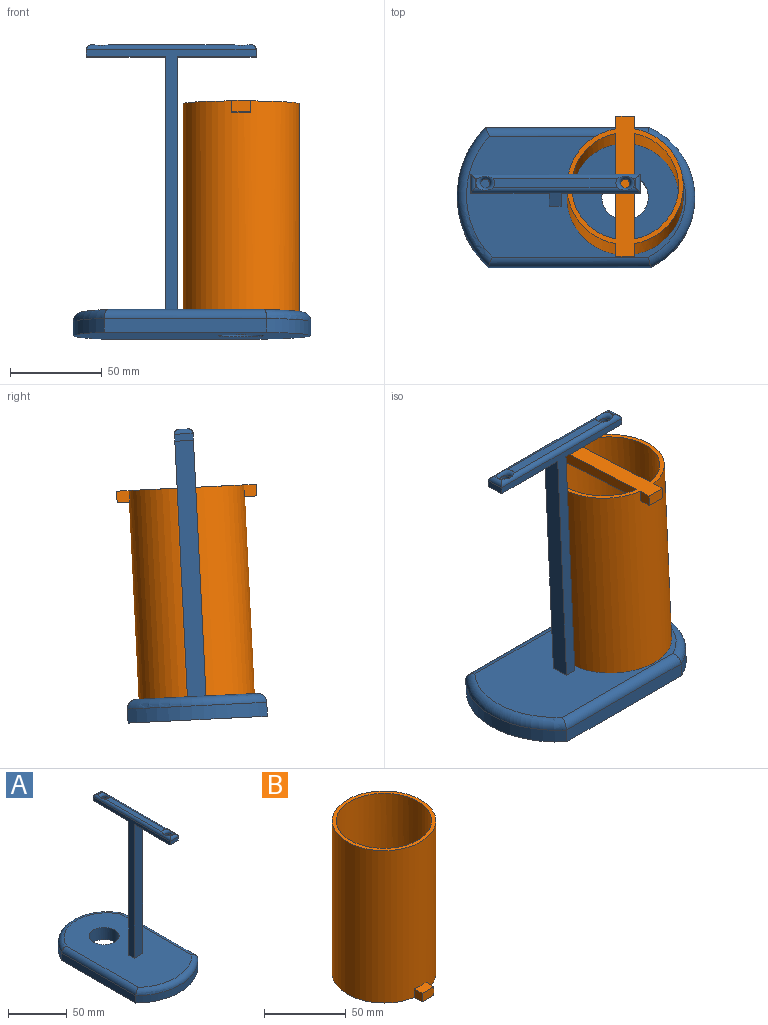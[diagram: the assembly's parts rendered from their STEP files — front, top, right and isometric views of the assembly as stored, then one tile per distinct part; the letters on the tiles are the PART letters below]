
ASSEMBLY  parts=2 mates=1
PART A: 30 faces, bbox 82.5x137.6x158.8 mm
  f0: plane 143.51x92.59mm, normal (1,0,0), area 1239.9mm2, adj f2,f3,f6,f7,f9,f12,f16,f23
  f1: plane 143.51x92.59mm, normal (-1,0,0), area 1239.9mm2, adj f2,f3,f6,f7,f9,f12,f17,f23
  f2: plane 139.7x10.16mm, normal (0,1,0), area 1419.4mm2, adj f0,f1,f12,f23
  f3: plane 139.7x10.16mm, normal (0,-1,0), area 1419.4mm2, adj f0,f1,f6,f23
  f4: plane 67.61x5.08mm, normal (0,0,1), area 338.8mm2, adj f15,f16,f17,f18
  f5: plane 5.08x1.15mm, normal (0,0,1), area 3.5mm2, adj f14,f15,f16,f17
  f6: plane 43.12x10.16mm, normal (0,0,-1), area 417.8mm2, adj f0,f1,f3,f9,f10
  f7: plane 10.16x3.81mm, normal (0,1,0), area 38.7mm2, adj f0,f1,f12,f14
  f8: cylinder r=2.54mm len=5.08mm, axis (0,0,-1), area 60.8mm2, adj f12,f15
  f9: plane 10.16x3.81mm, normal (0,-1,0), area 38.7mm2, adj f0,f1,f6,f13
  f10: cylinder r=2.54mm len=5.08mm, axis (0,0,-1), area 60.8mm2, adj f6,f18
  f11: plane 5.08x1.15mm, normal (0,0,1), area 3.5mm2, adj f13,f16,f17,f18
  f12: plane 43.12x10.16mm, normal (0,0,-1), area 417.8mm2, adj f0,f1,f2,f7,f8
  f13: cylinder r=2.54mm len=10.16mm, axis (-1,0,0), area 33.2mm2, adj f9,f11,f16,f17
  f14: cylinder r=2.54mm len=10.16mm, axis (1,0,0), area 33.2mm2, adj f5,f7,f16,f17
  f15: torus R=5.08mm, axis (0,0,1), area 69.5mm2, adj f4,f5,f8,f16,f17
  f16: cylinder r=2.54mm len=92.59mm, axis (0,-1,0), area 346.7mm2, adj f0,f4,f5,f11,f13,f14,f15,f18
  f17: cylinder r=2.54mm len=92.59mm, axis (0,1,0), area 346.7mm2, adj f1,f4,f5,f11,f13,f14,f15,f18
  f18: torus R=5.08mm, axis (0,0,1), area 69.5mm2, adj f4,f10,f11,f16,f17
  f19: cylinder r=52.78mm len=76.17mm, axis (0,0,-1), area 648.5mm2, adj f20,f22,f24,f28
  f20: plane 89.27x7.62mm, normal (-1,0,0), area 680.3mm2, adj f19,f21,f24,f29
  f21: cylinder r=41.78mm len=76.17mm, axis (0,0,-1), area 730.5mm2, adj f20,f22,f24,f27
  f22: plane 88.52x7.62mm, normal (1,0,0), area 674.5mm2, adj f19,f21,f24,f26
  f23: plane 119.6x66.01mm, normal (0,0,1), area 6662.4mm2, adj f0,f1,f2,f3,f25,f26,f27,f28
  f24: plane 129.76x76.17mm, normal (0,0,-1), area 8467.1mm2, adj f19,f20,f21,f22,f25
  f25: cylinder r=12.7mm len=25.4mm, axis (0,0,1), area 1013.4mm2, adj f23,f24
  f26: cylinder r=5.08mm len=88.52mm, axis (0,1,0), area 697.2mm2, adj f22,f23,f27,f28
  f27: torus R=36.7mm, axis (0,0,-1), area 724.9mm2, adj f21,f23,f26,f29
  f28: torus R=47.7mm, axis (0,0,-1), area 643.7mm2, adj f19,f23,f26,f29
  f29: cylinder r=5.08mm len=89.27mm, axis (0,-1,0), area 703mm2, adj f20,f23,f27,f28
PART B: 15 faces, bbox 63.5x76.4x114.3 mm
  f0: cylinder r=29.21mm len=114.3mm, axis (0,0,1), area 20848mm2, adj f2,f11,f12,f13,f14
  f1: cylinder r=31.75mm len=114.3mm, axis (0,0,1), area 22672.2mm2, adj f2,f3,f5,f6,f7,f8,f10,f14
  f2: plane 76.41x63.5mm, normal (0,0,-1), area 1210.9mm2, adj f0,f1,f3,f4,f5,f7,f8,f9
  f3: plane 6.86x6.35mm, normal (1,0,0), area 43.6mm2, adj f1,f2,f4,f6
  f4: plane 10.16x6.35mm, normal (0,-1,0), area 64.5mm2, adj f2,f3,f5,f6
  f5: plane 6.86x6.35mm, normal (-1,0,0), area 43.6mm2, adj f1,f2,f4,f6
  f6: plane 10.16x6.86mm, normal (0,0,1), area 66.9mm2, adj f1,f3,f4,f5
  f7: plane 6.86x6.35mm, normal (1,0,0), area 43.6mm2, adj f1,f2,f9,f10
  f8: plane 6.86x6.35mm, normal (-1,0,0), area 43.6mm2, adj f1,f2,f9,f10
  f9: plane 10.16x6.35mm, normal (0,1,0), area 64.5mm2, adj f2,f7,f8,f10
  f10: plane 10.16x6.86mm, normal (0,0,1), area 66.9mm2, adj f1,f7,f8,f9
  f11: plane 57.53x6.35mm, normal (1,0,0), area 365.3mm2, adj f0,f2,f13
  f12: plane 57.53x6.35mm, normal (-1,0,0), area 365.3mm2, adj f0,f2,f13
  f13: plane 58.42x10.16mm, normal (0,0,1), area 590.5mm2, adj f0,f11,f12
  f14: plane 63.5x63.5mm, normal (0,0,1), area 486.4mm2, adj f0,f1
PLACE A rot(axis=(-0.02,-0.02,-1),90deg) t=(-50.52,-72.4,96.08)mm
PLACE B rot(axis=(1,0,0),177.2deg) t=(-12.39,-42.35,-70.95)mm
MATE slider A.f25 <-> B.f0  axis (0,0.05,1) through (-12.39,-79.25,-43.45)mm
